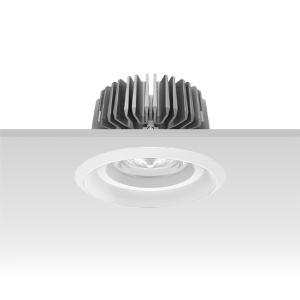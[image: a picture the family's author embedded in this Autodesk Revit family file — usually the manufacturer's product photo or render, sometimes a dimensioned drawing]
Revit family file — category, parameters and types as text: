
# Revit family: 3f_filippi_-_3f_reno_bianco_ampio_3f_filippi_-_30387_-_3f_reno_150_wh_3000-930_dali_wide
name_source: partatom
category: Lighting Fixtures
units: mm (PartAtom-declared; Revit-internal decimal feet)

## family parameters
Cut with Voids When Loaded = No
Host = Face
Light Source = No
Part Type = Normal
Room Calculation Point = No
Round Connector Dimension = Use Diameter
Shared = No

## types (1)
- 3F Filippi - 3F Reno Bianco Ampio (1 x LED, 2766 lm, 37 W, 3000 K)
    Apparent Load = 37 VA
    Approval mark = CE
    CIE Flux Codes = 76 95 100 100 100
    Color Rendering = 90
    Color Temperature = 3000 K
    Control Gear = Electronic transformer
    Default Elevation = 1800 mm
    Description = ILLUMINOTECHNICAL
Luminous efficiency 100% (DLOR 100%, ULOR 0%).
Initial luminous flux of the luminaire 2766 lm.
Direct symmetric wide distribution.
Installation Interdistance Transv.D = 1.54 x hu - Long.D = 1.54 x hu.
Tabular UGR (CIE 117 - 4H-8H; S=0.25H; 70/50/20): RUG 23.4 - 23.4.
Beam angle: 84° - 84°.
Luminous efficacy 75 lm/W.
Lifetime (L90/B10): 30000 h. (tq+25°C)
Lifetime (L85/B10): 50000 h. (tq+25°C)
Lifetime (L70/B10): 80000 h. (tq+25°C)
Sudden decreased luminous flux after 50000 hours: 0% (C0).
Photobiological safety in compliance with IEC/TR 62778: RG0 risk exempt, (IEC 62471).
In compliance with IEC/EN 62722-2-1 - IEC/EN 62717 standards.

SOURCE
Compact LED module 3000/930.
Energy efficiency class (UE 2019/2020 - UE 2019/2015): F.
CIE 13.3 Colour rendering index: CRI >90 (R9 >50%).
IES TM-30 Fidelity Index: Rf = 92 Rg = 101.
CCT nominal colour temperature 3000 K.
Colour initial tolerance (MacAdam): SDCM 3.
Zhaga Book 3 compliant.

MECHANICAL
Passive heat dissipator in die-casting aluminium, oversized, for optimum thermal management of the LED module.
Parabolic element with graduated/concentric rings in white polycarbonate.
Transparent external lens with glossy and satin differentiated surfaces, with a cooling and anti-insect system in methacrylate (PMMA).
Fastening spring clips in stainless steel.
Dimensions: diameter 166 mm, height 107 mm. Weight 1.39 kg.
IP44 protection degree for exposed part, IP20 for recessed part.
Mechanical strength to impacts IK04 (0.5 joule).
Glow-wire test resistance 650°C.

ELECTRICAL
Wiring on a separate unit.
Halogen Free DALI-2 DATI (Parts 251, 252, 253), PUSH-DIM, electronic wiring 230V-50/60Hz, power factor 0.97 at full load, THD <25%, constant output current, SELV, class II, 1 driver, 1 DALI addresse.
Power of the luminaire 37 W.
ENEC - CE.
SAFE FLICKER: PstLM=<1 and SVM=<0.4 (IEC TR 61547-1 and IEC TR 63158), to ensure a more comfortable and safe light.
Luminaire compliant with EN 60598-2-22 for power supply from a centralised emergency system CPSS (Central Power Supply System), not incorporated in the luminaire - high risk areas excluded. The default power and flux are 100% in AC and 100% in DC.
Ambient temperature from 0°C to +25°C.
Temperature class T6 max 85°C.
Relative humidity UR: <85%.

INSTALLATION
Pull-up recessed fitting.
False ceiling carving: 150 mm.
All accessories dedicated to this product are available on the Catalog and on our website www.3F-Filippi.com.

APPLICATIONS
Environments: architectural, commercial, exhibition areas, transit areas, corridors, shops, display windows, service areas.
In false ceilings with narrow voids.

LIGHT MANAGEMENT
Recommended minimum setting: 10%.
The luminaire, equipped with (DALI-2 DATI) driver, can be controlled manually with 3F Easy Dim technology or automatically/manually with wired or wireless DALI/D2D control systems.
The D2D driver guarantees interoperability with other devices with the same certification by making the following information available:
Device Data (Part 251), Energy Report (Part 252), Diagnosis & Maintenance (Part 253).
In electrical systems without a regulation system (manual or automatic) and DALI bus, a suitable jumper must be made on the DA-DA terminals of the appliance.

WARNING
Luminaire designed for disposal/recycling at end-of-life.
Replaceable (LED only) light source by a professional. Replaceable control gear by a professional.
    Height = 0 mm  [stored 0 ft]
    Lamp = 1 x LED
    Lamp Light Flux = 2766 lm
    Lamp Power = 37 W
    Lamp count = 1
    Length = 166 mm
    Lifetime = 50000 h
    Luminous efficacy = 75 lm/W
    Manufacturer = 3F Filippi
    ModVariant = No
    Model = 3F Filippi - 30387 - 3F Reno 150 WH 3000-930 DALI WIDE
    Mounting Place = Ceiling
    Mounting Type = Recessed
    Number of Poles = 1
    OnlyDefault = Yes
    Power Factor = 1
    Product Name = 3F Filippi - 3F Reno Bianco Ampio
    Product group = recessed luminaire
    ProductGroupID = 4
    Protection Class = Protection class II
    Protection Degree = IP 20
    RLX_Detail_Level = 1
    RLX_Emergency_Light_Flux = 0 lm
    RLX_Emergency_Type = 0
    RLX_Emergency_Type_DB = No
    RlxData = <blob elided: 85849 chars, md5=bad40efb>
    Socket = socket
    Standby Power = 0 W
    System Light Flux = 2766 lm
    System Power = 37 W
    Type Comments = Product without accessories
    Type Image = 3ffilippi_3f_reno_150_ampio_wh_3000_4000.jpg
    URL = http://relux.com
    VarID = ---
    Voltage = 0 V
    Weight = 0.00 kg
    Width = 0 mm  [stored 0 ft]

note: [stored X ft] marks values corroborated as IEEE doubles in the binary element streams (Revit-internal decimal feet)

## geometry (parser evidence)
native form markers: Blend x4, Sweep x12
no freeform markers — native parametric forms only
